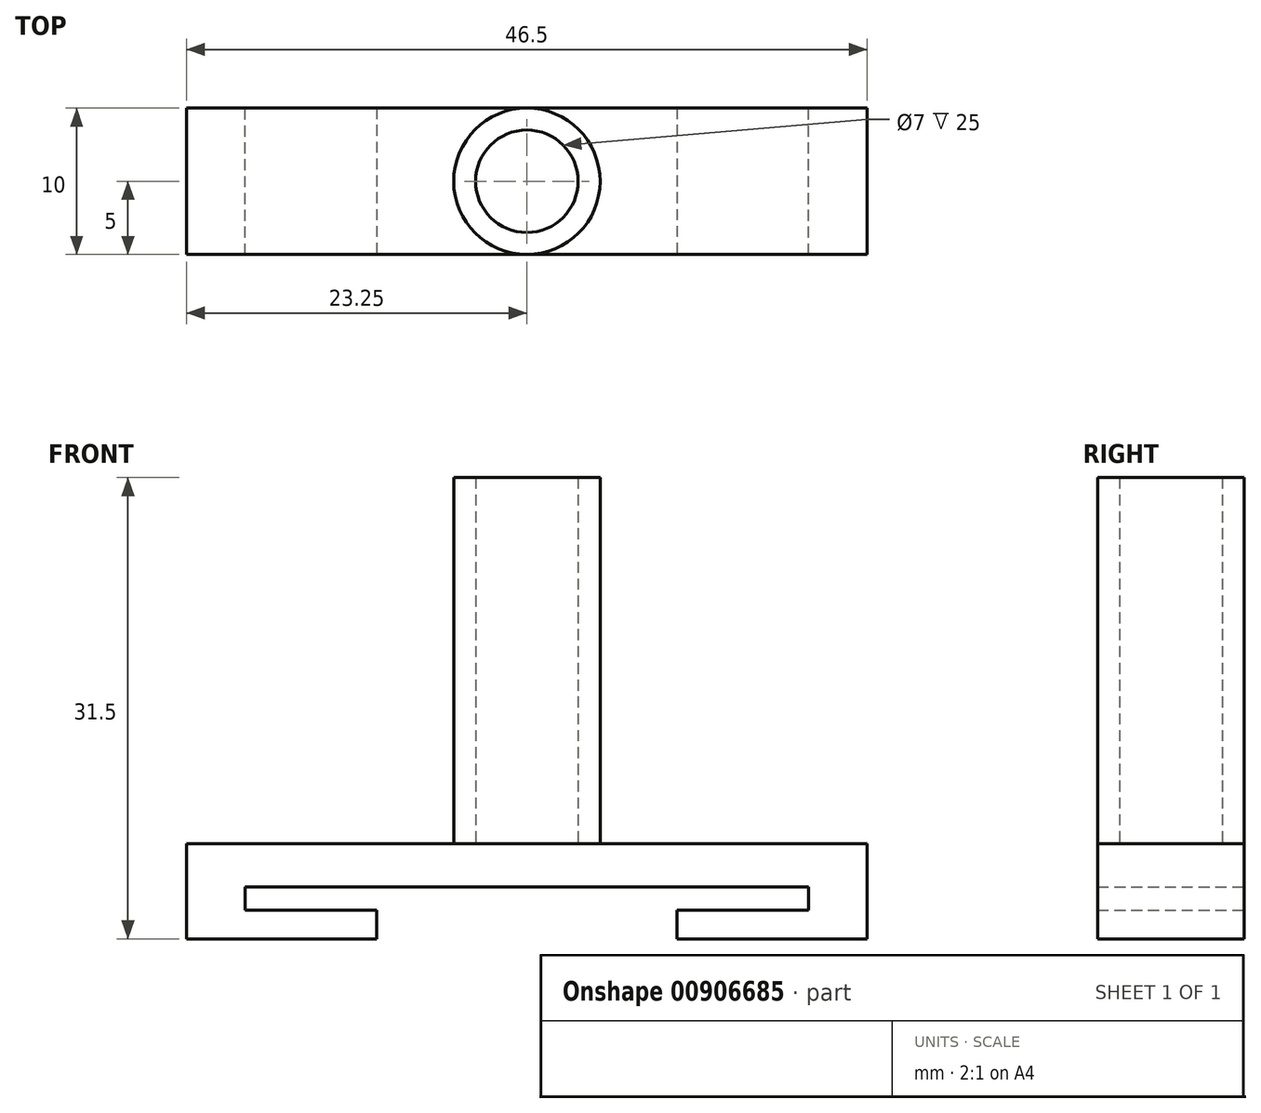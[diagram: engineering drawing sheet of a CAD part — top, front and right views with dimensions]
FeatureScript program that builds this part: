
annotation { "Feature Type Name" : "Feature", "Feature Type Description" : "" }
export const myFeature = defineFeature(function(context is Context, id is Id, definition is map)
    precondition{}
    {
        {
            var Q0;
            Q0=qCreatedBy(makeId("Top.planeOp"),FACE);
            var sketch = newSketch(context, id + "F0", { "sketchPlane" : qUnion([Q0])});
            skLineSegment(sketch, "E0.bottom", {"start": v(-19.25, 0) * mm, "end": v(19.25, 0) * mm});
            skLineSegment(sketch, "E0.top", {"start": v(-19.25, 10) * mm, "end": v(19.25, 10) * mm});
            skLineSegment(sketch, "E0.left", {"start": v(-19.25, 0) * mm, "end": v(-19.25, 10) * mm});
            skLineSegment(sketch, "E0.right", {"start": v(19.25, 0) * mm, "end": v(19.25, 10) * mm});
            skPoint(sketch, "E1", {"position": v(0, 0) * mm});
            skLineSegment(sketch, "E2", {"start": v(-19.25, 0) * mm, "end": v(-23.25, 0) * mm});
            skLineSegment(sketch, "E3", {"start": v(-23.25, 0) * mm, "end": v(-23.25, 10) * mm});
            skLineSegment(sketch, "E4", {"start": v(-23.25, 10) * mm, "end": v(23.25, 10) * mm});
            skLineSegment(sketch, "E5", {"start": v(23.25, 10) * mm, "end": v(23.25, 0) * mm});
            skLineSegment(sketch, "E6", {"start": v(23.25, 0) * mm, "end": v(19.25, 0) * mm});
            skLineSegment(sketch, "E7", {"start": v(-10.25, 10) * mm, "end": v(-10.25, 0) * mm});
            skLineSegment(sketch, "E8", {"start": v(10.25, 10) * mm, "end": v(10.25, 0) * mm});
            skSolve(sketch);
        }
        {
            var Q0;
            {var subQ0=sQuery(id+"F0.wireOp",EDGE,"E0.left");Q0=makeQuery(id+"F0.imprint","IMPRINT",FACE,{"disambiguationData":[TD([[makeQuery(id+"F0.imprint","IMPRINT",EDGE,{"derivedFrom":subQ0}),1.0]])]});}
            var Q1;
            {var subQ0=sQuery(id+"F0.wireOp",EDGE,"E0.left");Q1=makeQuery(id+"F0.imprint","IMPRINT",FACE,{"disambiguationData":[TD([[makeQuery(id+"F0.imprint","IMPRINT",EDGE,{"derivedFrom":subQ0}),-1.0]])]});}
            var Q2;
            {var subQ0=sQuery(id+"F0.wireOp",EDGE,"E7");Q2=makeQuery(id+"F0.imprint","IMPRINT",FACE,{"disambiguationData":[TD([[makeQuery(id+"F0.imprint","IMPRINT",EDGE,{"derivedFrom":subQ0}),1.0]])]});}
            var Q3;
            {var subQ0=sQuery(id+"F0.wireOp",EDGE,"E0.right");Q3=makeQuery(id+"F0.imprint","IMPRINT",FACE,{"disambiguationData":[TD([[makeQuery(id+"F0.imprint","IMPRINT",EDGE,{"derivedFrom":subQ0}),1.0]])]});}
            var Q4;
            {var subQ0=sQuery(id+"F0.wireOp",EDGE,"E0.right");Q4=makeQuery(id+"F0.imprint","IMPRINT",FACE,{"disambiguationData":[TD([[makeQuery(id+"F0.imprint","IMPRINT",EDGE,{"derivedFrom":subQ0}),-1.0]])]});}
            extrude(context, id + "F1", {"entities" : qUnion([Q0, Q1, Q2, Q3, Q4]), "depth" : 6.5 * mm, "offsetDistance" : 25 * mm});
        }
        {
            var Q0;
            {var subQ0=sQuery(id+"F0.wireOp",EDGE,"E0.left");Q0=makeQuery(id+"F0.imprint","IMPRINT",FACE,{"disambiguationData":[TD([[makeQuery(id+"F0.imprint","IMPRINT",EDGE,{"derivedFrom":subQ0}),-1.0]])]});}
            var Q1;
            {var subQ0=sQuery(id+"F0.wireOp",EDGE,"E7");Q1=makeQuery(id+"F0.imprint","IMPRINT",FACE,{"disambiguationData":[TD([[makeQuery(id+"F0.imprint","IMPRINT",EDGE,{"derivedFrom":subQ0}),1.0]])]});}
            var Q2;
            {var subQ0=sQuery(id+"F0.wireOp",EDGE,"E0.right");Q2=makeQuery(id+"F0.imprint","IMPRINT",FACE,{"disambiguationData":[TD([[makeQuery(id+"F0.imprint","IMPRINT",EDGE,{"derivedFrom":subQ0}),1.0]])]});}
            extrude(context, id + "F2", {"entities" : qUnion([Q0, Q1, Q2]), "operationType" : NewBodyOperationType.REMOVE, "depth" : 3.55 * mm, "offsetDistance" : 25 * mm});
        }
        {
            var Q0;
            {var subQ0=sQuery(id+"F0.wireOp",EDGE,"E0.left");Q0=makeQuery(id+"F0.imprint","IMPRINT",FACE,{"disambiguationData":[TD([[makeQuery(id+"F0.imprint","IMPRINT",EDGE,{"derivedFrom":subQ0}),-1.0]])]});}
            var Q1;
            {var subQ0=sQuery(id+"F0.wireOp",EDGE,"E0.right");Q1=makeQuery(id+"F0.imprint","IMPRINT",FACE,{"disambiguationData":[TD([[makeQuery(id+"F0.imprint","IMPRINT",EDGE,{"derivedFrom":subQ0}),1.0]])]});}
            extrude(context, id + "F3", {"entities" : qUnion([Q0, Q1]), "operationType" : NewBodyOperationType.ADD, "depth" : 1.95 * mm, "offsetDistance" : 25 * mm});
        }
        {
            var Q0;
            Q0=makeQuery(id+"F1.opExtrude","CAP_FACE",FACE,{"disambiguationData":[OSD([sQuery(id+"F0.wireOp",EDGE,"E0.bottom"),sQuery(id+"F0.wireOp",EDGE,"E2"),sQuery(id+"F0.wireOp",EDGE,"E3"),sQuery(id+"F0.wireOp",EDGE,"E4"),sQuery(id+"F0.wireOp",EDGE,"E5"),sQuery(id+"F0.wireOp",EDGE,"E6")])],"isStart":false});
            var sketch = newSketch(context, id + "F4", { "sketchPlane" : qUnion([Q0])});
            skCircle(sketch, "E9", {"center": v(0, 5) * mm, "radius": 5 * mm});
            skLineSegment(sketch, "E10", {"start": v(0, 0) * mm, "end": v(0, 10) * mm, "construction": true});
            skCircle(sketch, "E11", {"center": v(0, 5) * mm, "radius": 3.5 * mm});
            skSolve(sketch);
        }
        {
            var Q0;
            {var subQ0=sQuery(id+"F4.wireOp",EDGE,"E9");var subQ2=makeQuery(id+"F4.imprint","INTERSECT",VERTEX,{"derivedFrom":[makeQuery(id+"F1.opExtrude","CAP_EDGE",EDGE,{"disambiguationData":[OSD([sQuery(id+"F0.wireOp",EDGE,"E4")])],"isStart":false}),subQ0]});Q0=makeQuery(id+"F4.imprint","IMPRINT",FACE,{"disambiguationData":[TD([[makeQuery(id+"F4.imprint","IMPRINT",EDGE,{"disambiguationData":[TD([[subQ2,-1.0]])],"derivedFrom":subQ0}),1.0]])]});}
            extrude(context, id + "F5", {"entities" : qUnion([Q0]), "operationType" : NewBodyOperationType.ADD, "depth" : 25 * mm, "offsetDistance" : 25 * mm});
        }
    });
